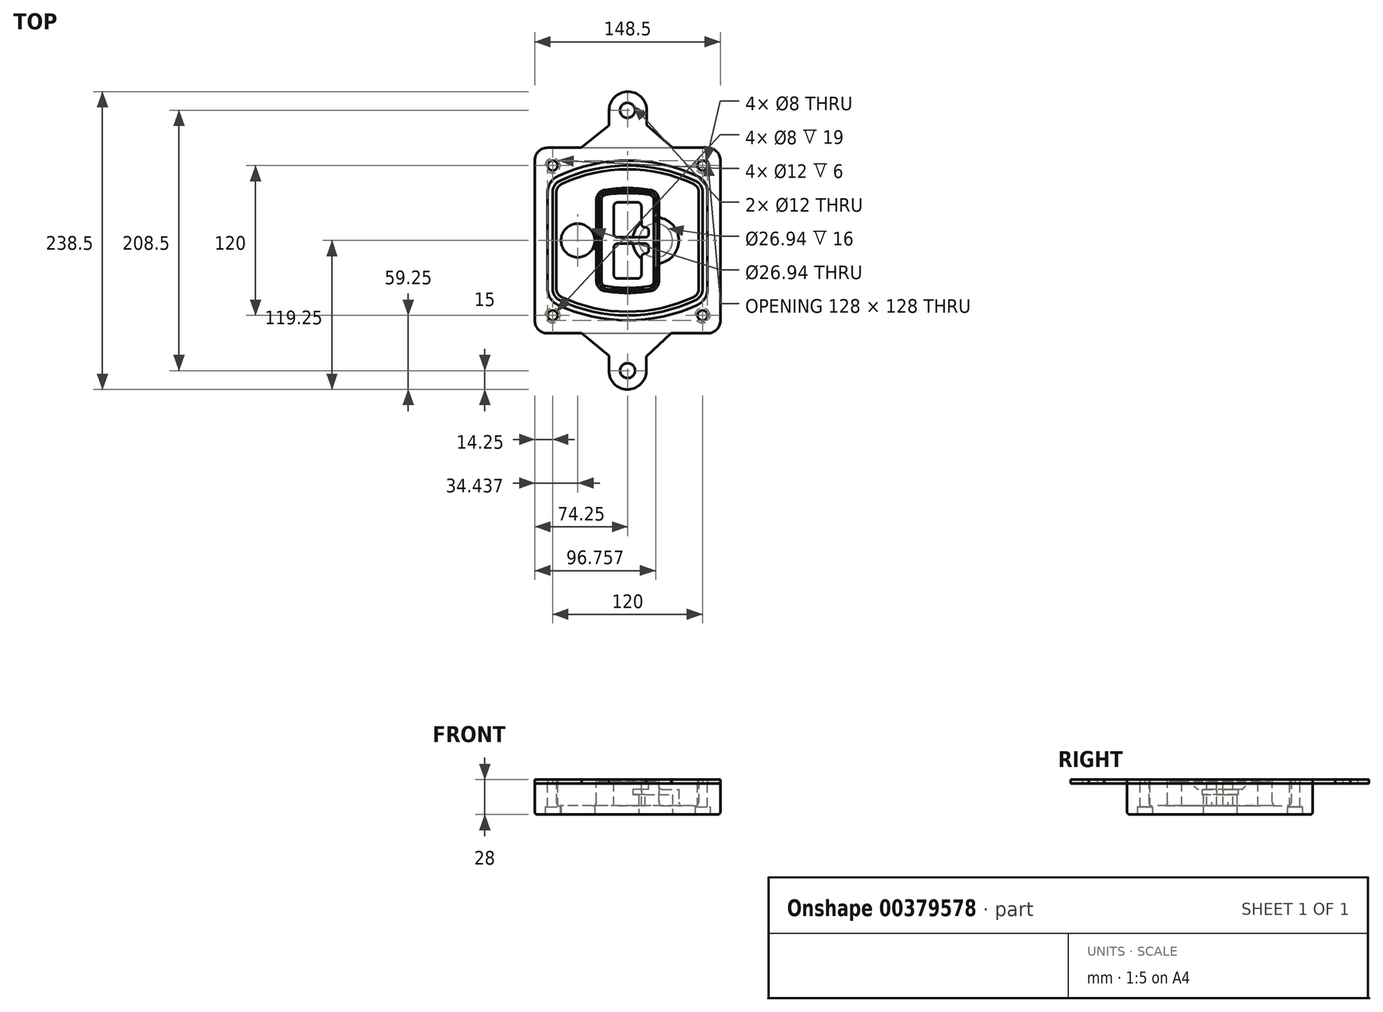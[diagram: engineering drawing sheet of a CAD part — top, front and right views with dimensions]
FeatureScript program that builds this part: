
annotation { "Feature Type Name" : "Feature", "Feature Type Description" : "" }
export const myFeature = defineFeature(function(context is Context, id is Id, definition is map)
    precondition{}
    {
        {
            var Q0;
            Q0=qCreatedBy(makeId("Top.planeOp"),FACE);
            var sketch = newSketch(context, id + "F0", { "sketchPlane" : qUnion([Q0])});
            skPoint(sketch, "E0.rect.middle", {"position": v(0, 0) * mm});
            skLineSegment(sketch, "E1.bottom", {"start": v(-64.25, -74.25) * mm, "end": v(64.25, -74.25) * mm});
            skLineSegment(sketch, "E1.top", {"start": v(-64.25, 74.25) * mm, "end": v(64.25, 74.25) * mm});
            skLineSegment(sketch, "E1.left", {"start": v(-74.25, -64.25) * mm, "end": v(-74.25, 64.25) * mm});
            skLineSegment(sketch, "E1.right", {"start": v(74.25, -64.25) * mm, "end": v(74.25, 64.25) * mm});
            skLineSegment(sketch, "E2", {"start": v(-74.25, 74.25) * mm, "end": v(74.25, -74.25) * mm, "construction": true});
            skLineSegment(sketch, "E3", {"start": v(74.25, 74.25) * mm, "end": v(-74.25, -74.25) * mm, "construction": true});
            skCircle(sketch, "E4", {"center": v(-60, 60) * mm, "radius": 4 * mm});
            skCircle(sketch, "E5", {"center": v(60, 60) * mm, "radius": 4 * mm});
            skCircle(sketch, "E6", {"center": v(60, -60) * mm, "radius": 4 * mm});
            skCircle(sketch, "E7", {"center": v(-60, -60) * mm, "radius": 4 * mm});
            skLineSegment(sketch, "E8", {"start": v(-60, 60) * mm, "end": v(60, 60) * mm, "construction": true});
            skLineSegment(sketch, "E9", {"start": v(60, 60) * mm, "end": v(60, -60) * mm, "construction": true});
            skLineSegment(sketch, "E10", {"start": v(60, -60) * mm, "end": v(-60, -60) * mm, "construction": true});
            skLineSegment(sketch, "E11", {"start": v(-60, -60) * mm, "end": v(-60, 60) * mm, "construction": true});
            skLineSegment(sketch, "E12", {"start": v(-60, 38.83) * mm, "end": v(-60, -38.83) * mm});
            skLineSegment(sketch, "E13", {"start": v(60, 38.83) * mm, "end": v(60, -38.83) * mm});
            skArc(sketch, "E14", {"start": v(54.26, 47.88) * mm, "mid": v(0, 60) * mm, "end": v(-54.26, 47.88) * mm});
            skArc(sketch, "E15", {"start": v(-54.26, -47.88) * mm, "mid": v(0, -60) * mm, "end": v(54.26, -47.88) * mm});
            skLineSegment(sketch, "E16", {"start": v(-60, 0) * mm, "end": v(60, 0) * mm, "construction": true});
            skPoint(sketch, "E17.visualSharp", {"position": v(-60, -45) * mm});
            skArc(sketch, "E17.filletArc", {"start": v(-60, -38.83) * mm, "mid": v(-58.44, -44.2) * mm, "end": v(-54.26, -47.88) * mm});
            skPoint(sketch, "E18.visualSharp", {"position": v(-60, 45) * mm});
            skArc(sketch, "E18.filletArc", {"start": v(-54.26, 47.88) * mm, "mid": v(-58.44, 44.2) * mm, "end": v(-60, 38.83) * mm});
            skPoint(sketch, "E19.visualSharp", {"position": v(60, 45) * mm});
            skArc(sketch, "E19.filletArc", {"start": v(60, 38.83) * mm, "mid": v(58.44, 44.2) * mm, "end": v(54.26, 47.88) * mm});
            skPoint(sketch, "E20.visualSharp", {"position": v(60, -45) * mm});
            skArc(sketch, "E20.filletArc", {"start": v(54.26, -47.88) * mm, "mid": v(58.44, -44.2) * mm, "end": v(60, -38.83) * mm});
            skPoint(sketch, "E21.visualSharp", {"position": v(-74.25, 74.25) * mm});
            skArc(sketch, "E21.filletArc", {"start": v(-64.25, 74.25) * mm, "mid": v(-71.32, 71.32) * mm, "end": v(-74.25, 64.25) * mm});
            skPoint(sketch, "E22.visualSharp", {"position": v(74.25, 74.25) * mm});
            skArc(sketch, "E22.filletArc", {"start": v(74.25, 64.25) * mm, "mid": v(71.32, 71.32) * mm, "end": v(64.25, 74.25) * mm});
            skPoint(sketch, "E23.visualSharp", {"position": v(74.25, -74.25) * mm});
            skArc(sketch, "E23.filletArc", {"start": v(64.25, -74.25) * mm, "mid": v(71.32, -71.32) * mm, "end": v(74.25, -64.25) * mm});
            skPoint(sketch, "E24.visualSharp", {"position": v(-74.25, -74.25) * mm});
            skArc(sketch, "E24.filletArc", {"start": v(-74.25, -64.25) * mm, "mid": v(-71.32, -71.32) * mm, "end": v(-64.25, -74.25) * mm});
            skArc(sketch, "E25.0", {"start": v(57, 38.83) * mm, "mid": v(55.9, 42.58) * mm, "end": v(52.98, 45.17) * mm});
            skLineSegment(sketch, "E25.1", {"start": v(57, 38.83) * mm, "end": v(57, -38.83) * mm});
            skArc(sketch, "E25.2", {"start": v(52.98, -45.17) * mm, "mid": v(55.9, -42.58) * mm, "end": v(57, -38.83) * mm});
            skArc(sketch, "E25.3", {"start": v(-52.98, -45.17) * mm, "mid": v(0, -57) * mm, "end": v(52.98, -45.17) * mm});
            skArc(sketch, "E25.4", {"start": v(-57, -38.83) * mm, "mid": v(-55.9, -42.58) * mm, "end": v(-52.98, -45.17) * mm});
            skArc(sketch, "E25.5", {"start": v(52.98, 45.17) * mm, "mid": v(0, 57) * mm, "end": v(-52.98, 45.17) * mm});
            skLineSegment(sketch, "E25.6", {"start": v(-57, 38.83) * mm, "end": v(-57, -38.83) * mm});
            skArc(sketch, "E25.7", {"start": v(-52.98, 45.17) * mm, "mid": v(-55.9, 42.58) * mm, "end": v(-57, 38.83) * mm});
            skArc(sketch, "E26.0", {"start": v(-55.96, 51.5) * mm, "mid": v(-61.82, 46.33) * mm, "end": v(-64, 38.83) * mm});
            skArc(sketch, "E26.1", {"start": v(55.96, 51.5) * mm, "mid": v(0, 64) * mm, "end": v(-55.96, 51.5) * mm});
            skArc(sketch, "E26.2", {"start": v(64, 38.83) * mm, "mid": v(61.82, 46.33) * mm, "end": v(55.96, 51.5) * mm});
            skLineSegment(sketch, "E26.3", {"start": v(64, 38.83) * mm, "end": v(64, -38.83) * mm});
            skArc(sketch, "E26.4", {"start": v(55.96, -51.5) * mm, "mid": v(61.82, -46.33) * mm, "end": v(64, -38.83) * mm});
            skLineSegment(sketch, "E26.5", {"start": v(-64, 38.83) * mm, "end": v(-64, -38.83) * mm});
            skArc(sketch, "E26.6", {"start": v(-55.96, -51.5) * mm, "mid": v(0, -64) * mm, "end": v(55.96, -51.5) * mm});
            skArc(sketch, "E26.7", {"start": v(-64, -38.83) * mm, "mid": v(-61.82, -46.33) * mm, "end": v(-55.96, -51.5) * mm});
            skPoint(sketch, "E27.endSnap0", {"position": v(0, 74.25) * mm});
            skLineSegment(sketch, "E28", {"start": v(0, 74.25) * mm, "end": v(0, 104.25) * mm});
            skCircle(sketch, "E29", {"center": v(0, 104.25) * mm, "radius": 6 * mm});
            skLineSegment(sketch, "E30", {"start": v(-37.03, 74.25) * mm, "end": v(-14.76, 92.25) * mm});
            skLineSegment(sketch, "E31", {"start": v(36.07, 74.25) * mm, "end": v(15.24, 92.42) * mm});
            skLineSegment(sketch, "E32", {"start": v(-14.76, 92.25) * mm, "end": v(-14.76, 104.25) * mm});
            skLineSegment(sketch, "E33", {"start": v(15.24, 92.42) * mm, "end": v(15.24, 104.42) * mm});
            skLineSegment(sketch, "E34", {"start": v(-60.73, 104.25) * mm, "end": v(-60.73, 74.25) * mm});
            skArc(sketch, "E35", {"start": v(-14.76, 104.25) * mm, "mid": v(0.16, 119.25) * mm, "end": v(15.24, 104.42) * mm});
            skLineSegment(sketch, "E36", {"start": v(0, -74.25) * mm, "end": v(0, -104.25) * mm});
            skCircle(sketch, "E37", {"center": v(0, -104.25) * mm, "radius": 6 * mm});
            skLineSegment(sketch, "E38", {"start": v(34.92, -74.25) * mm, "end": v(15, -92.78) * mm});
            skLineSegment(sketch, "E39", {"start": v(15, -92.78) * mm, "end": v(15, -104.78) * mm});
            skLineSegment(sketch, "E40", {"start": v(-36.77, -74.25) * mm, "end": v(-15, -92.25) * mm});
            skLineSegment(sketch, "E41", {"start": v(-15, -92.25) * mm, "end": v(-15, -104.25) * mm});
            skArc(sketch, "E42", {"start": v(-15, -104.25) * mm, "mid": v(-0.26, -119.25) * mm, "end": v(15, -104.78) * mm});
            skSolve(sketch);
        }
        {
            var Q0;
            Q0=makeQuery(id+"F0.imprint","IMPRINT",FACE,{"disambiguationData":[TD([[makeQuery(id+"F0.imprint","IMPRINT",EDGE,{"derivedFrom":sQuery(id+"F0.wireOp",EDGE,"E1.bottom")}),1.0]])]});
            var Q1;
            Q1=makeQuery(id+"F0.imprint","IMPRINT",FACE,{"disambiguationData":[TD([[makeQuery(id+"F0.imprint","IMPRINT",EDGE,{"derivedFrom":sQuery(id+"F0.wireOp",EDGE,"E12")}),1.0]])]});
            var Q2;
            Q2=makeQuery(id+"F0.imprint","IMPRINT",FACE,{"disambiguationData":[TD([[makeQuery(id+"F0.imprint","IMPRINT",EDGE,{"derivedFrom":sQuery(id+"F0.wireOp",EDGE,"E25.0")}),1.0]])]});
            var Q3;
            Q3=makeQuery(id+"F0.imprint","IMPRINT",FACE,{"disambiguationData":[TD([[makeQuery(id+"F0.imprint","IMPRINT",EDGE,{"derivedFrom":sQuery(id+"F0.wireOp",EDGE,"E12")}),-1.0]])]});
            extrude(context, id + "F1", {"entities" : qUnion([Q0, Q1, Q2, Q3]), "oppositeDirection" : true, "depth" : 25 * mm});
        }
        {
            var Q0;
            Q0=makeQuery(id+"F0.imprint","IMPRINT",FACE,{"disambiguationData":[TD([[makeQuery(id+"F0.imprint","IMPRINT",EDGE,{"derivedFrom":sQuery(id+"F0.wireOp",EDGE,"E12")}),1.0]])]});
            extrude(context, id + "F2", {"entities" : qUnion([Q0]), "operationType" : NewBodyOperationType.ADD, "depth" : 3 * mm});
        }
        {
            var Q0;
            Q0=makeQuery(id+"F0.imprint","IMPRINT",FACE,{"disambiguationData":[TD([[makeQuery(id+"F0.imprint","IMPRINT",EDGE,{"derivedFrom":sQuery(id+"F0.wireOp",EDGE,"E25.0")}),1.0]])]});
            extrude(context, id + "F3", {"entities" : qUnion([Q0]), "operationType" : NewBodyOperationType.REMOVE, "oppositeDirection" : true, "depth" : 18 * mm});
        }
        {
            var Q0;
            Q0=makeQuery(id+"F2.opExtrude","CAP_FACE",FACE,{"disambiguationData":[OSD([sQuery(id+"F0.wireOp",EDGE,"E12"),sQuery(id+"F0.wireOp",EDGE,"E13"),sQuery(id+"F0.wireOp",EDGE,"E14"),sQuery(id+"F0.wireOp",EDGE,"E15"),sQuery(id+"F0.wireOp",EDGE,"E17.filletArc"),sQuery(id+"F0.wireOp",EDGE,"E18.filletArc"),sQuery(id+"F0.wireOp",EDGE,"E19.filletArc"),sQuery(id+"F0.wireOp",EDGE,"E20.filletArc"),sQuery(id+"F0.wireOp",EDGE,"E25.0"),sQuery(id+"F0.wireOp",EDGE,"E25.1"),sQuery(id+"F0.wireOp",EDGE,"E25.2"),sQuery(id+"F0.wireOp",EDGE,"E25.3"),sQuery(id+"F0.wireOp",EDGE,"E25.4"),sQuery(id+"F0.wireOp",EDGE,"E25.5"),sQuery(id+"F0.wireOp",EDGE,"E25.6"),sQuery(id+"F0.wireOp",EDGE,"E25.7")])],"isStart":false});
            var sketch = newSketch(context, id + "F4", { "sketchPlane" : qUnion([Q0])});
            skArc(sketch, "E43.0", {"start": v(-18.34, -40.45) * mm, "mid": v(0, -42) * mm, "end": v(18.34, -40.45) * mm});
            skArc(sketch, "E44.0", {"start": v(18.34, 40.45) * mm, "mid": v(0, 42) * mm, "end": v(-18.34, 40.45) * mm});
            skLineSegment(sketch, "E45", {"start": v(-25, 32.57) * mm, "end": v(-25, -32.57) * mm});
            skLineSegment(sketch, "E46", {"start": v(25, 32.57) * mm, "end": v(25, -32.57) * mm});
            skLineSegment(sketch, "E47", {"start": v(-25, 39.1) * mm, "end": v(25, 39.1) * mm, "construction": true});
            skLineSegment(sketch, "E48", {"start": v(-25, -39.1) * mm, "end": v(25, -39.1) * mm, "construction": true});
            skPoint(sketch, "E49.visualSharp", {"position": v(-25, 39.1) * mm});
            skArc(sketch, "E49.filletArc", {"start": v(-18.34, 40.45) * mm, "mid": v(-23.11, 37.73) * mm, "end": v(-25, 32.57) * mm});
            skPoint(sketch, "E50.visualSharp", {"position": v(25, 39.1) * mm});
            skArc(sketch, "E50.filletArc", {"start": v(25, 32.57) * mm, "mid": v(23.11, 37.73) * mm, "end": v(18.34, 40.45) * mm});
            skPoint(sketch, "E51.visualSharp", {"position": v(25, -39.1) * mm});
            skArc(sketch, "E51.filletArc", {"start": v(18.34, -40.45) * mm, "mid": v(23.11, -37.73) * mm, "end": v(25, -32.57) * mm});
            skPoint(sketch, "E52.visualSharp", {"position": v(-25, -39.1) * mm});
            skArc(sketch, "E52.filletArc", {"start": v(-25, -32.57) * mm, "mid": v(-23.11, -37.73) * mm, "end": v(-18.34, -40.45) * mm});
            skArc(sketch, "E53.0", {"start": v(52.98, 45.17) * mm, "mid": v(0, 57) * mm, "end": v(-52.98, 45.17) * mm});
            skArc(sketch, "E53.1", {"start": v(-52.98, 45.17) * mm, "mid": v(-55.9, 42.58) * mm, "end": v(-57, 38.83) * mm});
            skLineSegment(sketch, "E53.2", {"start": v(-57, 38.83) * mm, "end": v(-57, -38.83) * mm});
            skArc(sketch, "E53.3", {"start": v(-57, -38.83) * mm, "mid": v(-55.9, -42.58) * mm, "end": v(-52.98, -45.17) * mm});
            skArc(sketch, "E53.4", {"start": v(-52.98, -45.17) * mm, "mid": v(0, -57) * mm, "end": v(52.98, -45.17) * mm});
            skArc(sketch, "E53.5", {"start": v(52.98, -45.17) * mm, "mid": v(55.9, -42.58) * mm, "end": v(57, -38.83) * mm});
            skLineSegment(sketch, "E53.6", {"start": v(57, 38.83) * mm, "end": v(57, -38.83) * mm});
            skArc(sketch, "E53.7", {"start": v(57, 38.83) * mm, "mid": v(55.9, 42.58) * mm, "end": v(52.98, 45.17) * mm});
            skLineSegment(sketch, "E54.0", {"start": v(23, 32.57) * mm, "end": v(23, -32.57) * mm});
            skArc(sketch, "E54.1", {"start": v(18, -38.48) * mm, "mid": v(21.58, -36.44) * mm, "end": v(23, -32.57) * mm});
            skArc(sketch, "E54.2", {"start": v(-18, -38.48) * mm, "mid": v(0, -40) * mm, "end": v(18, -38.48) * mm});
            skArc(sketch, "E54.3", {"start": v(-23, -32.57) * mm, "mid": v(-21.58, -36.44) * mm, "end": v(-18, -38.48) * mm});
            skLineSegment(sketch, "E54.4", {"start": v(-23, 32.57) * mm, "end": v(-23, -32.57) * mm});
            skArc(sketch, "E54.5", {"start": v(23, 32.57) * mm, "mid": v(21.58, 36.44) * mm, "end": v(18, 38.48) * mm});
            skArc(sketch, "E54.6", {"start": v(-18, 38.48) * mm, "mid": v(-21.58, 36.44) * mm, "end": v(-23, 32.57) * mm});
            skArc(sketch, "E54.7", {"start": v(18, 38.48) * mm, "mid": v(0, 40) * mm, "end": v(-18, 38.48) * mm});
            skArc(sketch, "E55.0", {"start": v(21, 32.57) * mm, "mid": v(20.06, 35.15) * mm, "end": v(17.67, 36.5) * mm});
            skLineSegment(sketch, "E55.1", {"start": v(21, 32.57) * mm, "end": v(21, -32.57) * mm});
            skArc(sketch, "E55.2", {"start": v(17.67, -36.5) * mm, "mid": v(20.06, -35.15) * mm, "end": v(21, -32.57) * mm});
            skArc(sketch, "E55.3", {"start": v(-17.67, -36.5) * mm, "mid": v(0, -38) * mm, "end": v(17.67, -36.5) * mm});
            skArc(sketch, "E55.4", {"start": v(-21, -32.57) * mm, "mid": v(-20.06, -35.15) * mm, "end": v(-17.67, -36.5) * mm});
            skArc(sketch, "E55.5", {"start": v(17.67, 36.5) * mm, "mid": v(0, 38) * mm, "end": v(-17.67, 36.5) * mm});
            skLineSegment(sketch, "E55.6", {"start": v(-21, 32.57) * mm, "end": v(-21, -32.57) * mm});
            skArc(sketch, "E55.7", {"start": v(-17.67, 36.5) * mm, "mid": v(-20.06, 35.15) * mm, "end": v(-21, 32.57) * mm});
            skLineSegment(sketch, "E56", {"start": v(-25, 0) * mm, "end": v(25, 0) * mm, "construction": true});
            skLineSegment(sketch, "E57", {"start": v(-11, 5.5) * mm, "end": v(-11, 27.5) * mm});
            skLineSegment(sketch, "E58", {"start": v(-8, 30.5) * mm, "end": v(8, 30.5) * mm});
            skLineSegment(sketch, "E59", {"start": v(11, 27.5) * mm, "end": v(11, 13.5) * mm});
            skLineSegment(sketch, "E60", {"start": v(14, 10.5) * mm, "end": v(14, 10.5) * mm});
            skLineSegment(sketch, "E61", {"start": v(17, 7.5) * mm, "end": v(17, 5.5) * mm});
            skLineSegment(sketch, "E62", {"start": v(14, 2.5) * mm, "end": v(-8, 2.5) * mm});
            skPoint(sketch, "E63.visualSharp", {"position": v(-11, 30.5) * mm});
            skArc(sketch, "E63.filletArc", {"start": v(-8, 30.5) * mm, "mid": v(-10.12, 29.62) * mm, "end": v(-11, 27.5) * mm});
            skPoint(sketch, "E64.visualSharp", {"position": v(11, 30.5) * mm});
            skArc(sketch, "E64.filletArc", {"start": v(11, 27.5) * mm, "mid": v(10.12, 29.62) * mm, "end": v(8, 30.5) * mm});
            skPoint(sketch, "E65.visualSharp", {"position": v(11, 10.5) * mm});
            skArc(sketch, "E65.filletArc", {"start": v(11, 13.5) * mm, "mid": v(11.88, 11.38) * mm, "end": v(14, 10.5) * mm});
            skPoint(sketch, "E66.visualSharp", {"position": v(17, 10.5) * mm});
            skArc(sketch, "E66.filletArc", {"start": v(17, 7.5) * mm, "mid": v(16.12, 9.62) * mm, "end": v(14, 10.5) * mm});
            skPoint(sketch, "E67.visualSharp", {"position": v(17, 2.5) * mm});
            skArc(sketch, "E67.filletArc", {"start": v(14, 2.5) * mm, "mid": v(16.12, 3.38) * mm, "end": v(17, 5.5) * mm});
            skPoint(sketch, "E68.visualSharp", {"position": v(-11, 2.5) * mm});
            skArc(sketch, "E68.filletArc", {"start": v(-11, 5.5) * mm, "mid": v(-10.12, 3.38) * mm, "end": v(-8, 2.5) * mm});
            skLineSegment(sketch, "E69.0.MirrorCS", {"start": v(14, -2.5) * mm, "end": v(-8, -2.5) * mm});
            skArc(sketch, "E70.0.MirrorCS", {"start": v(-11, -5.5) * mm, "mid": v(-10.12, -3.38) * mm, "end": v(-8, -2.5) * mm});
            skLineSegment(sketch, "E71.0.MirrorCS", {"start": v(-11, -5.5) * mm, "end": v(-11, -27.5) * mm});
            skArc(sketch, "E72.0.MirrorCS", {"start": v(-8, -30.5) * mm, "mid": v(-10.12, -29.62) * mm, "end": v(-11, -27.5) * mm});
            skLineSegment(sketch, "E73.0.MirrorCS", {"start": v(-8, -30.5) * mm, "end": v(8, -30.5) * mm});
            skArc(sketch, "E74.0.MirrorCS", {"start": v(11, -27.5) * mm, "mid": v(10.12, -29.62) * mm, "end": v(8, -30.5) * mm});
            skLineSegment(sketch, "E75.0.MirrorCS", {"start": v(11, -27.5) * mm, "end": v(11, -13.5) * mm});
            skArc(sketch, "E76.0.MirrorCS", {"start": v(11, -13.5) * mm, "mid": v(11.88, -11.38) * mm, "end": v(14, -10.5) * mm});
            skArc(sketch, "E77.0.MirrorCS", {"start": v(17, -7.5) * mm, "mid": v(16.12, -9.62) * mm, "end": v(14, -10.5) * mm});
            skLineSegment(sketch, "E78.0.MirrorCS", {"start": v(17, -7.5) * mm, "end": v(17, -5.5) * mm});
            skArc(sketch, "E79.0.MirrorCS", {"start": v(14, -2.5) * mm, "mid": v(16.12, -3.38) * mm, "end": v(17, -5.5) * mm});
            skSolve(sketch);
        }
        {
            var Q0;
            Q0=makeQuery(id+"F4.imprint","IMPRINT",FACE,{"disambiguationData":[TD([[makeQuery(id+"F4.imprint","IMPRINT",EDGE,{"derivedFrom":sQuery(id+"F4.wireOp",EDGE,"E43.0")}),1.0]])]});
            var Q1;
            Q1=makeQuery(id+"F4.imprint","IMPRINT",FACE,{"disambiguationData":[TD([[makeQuery(id+"F4.imprint","IMPRINT",EDGE,{"derivedFrom":sQuery(id+"F4.wireOp",EDGE,"E54.0")}),-1.0]])]});
            var Q2;
            Q2=makeQuery(id+"F4.imprint","IMPRINT",FACE,{"disambiguationData":[TD([[makeQuery(id+"F4.imprint","IMPRINT",EDGE,{"derivedFrom":sQuery(id+"F4.wireOp",EDGE,"E55.0")}),1.0]])]});
            extrude(context, id + "F5", {"entities" : qUnion([Q0, Q1, Q2]), "operationType" : NewBodyOperationType.ADD, "endBound" : BoundingType.UP_TO_NEXT, "oppositeDirection" : true, "depth" : 25 * mm});
        }
        {
            var Q0;
            Q0=makeQuery(id+"F4.imprint","IMPRINT",FACE,{"disambiguationData":[TD([[makeQuery(id+"F4.imprint","IMPRINT",EDGE,{"derivedFrom":sQuery(id+"F4.wireOp",EDGE,"E54.0")}),-1.0]])]});
            extrude(context, id + "F6", {"entities" : qUnion([Q0]), "operationType" : NewBodyOperationType.REMOVE, "oppositeDirection" : true, "depth" : 2 * mm});
        }
        {
            var Q0;
            Q0=makeQuery(id+"F1.opExtrude","CAP_FACE",FACE,{"disambiguationData":[OSD([sQuery(id+"F0.wireOp",EDGE,"E1.bottom"),sQuery(id+"F0.wireOp",EDGE,"E1.top"),sQuery(id+"F0.wireOp",EDGE,"E1.left"),sQuery(id+"F0.wireOp",EDGE,"E1.right"),sQuery(id+"F0.wireOp",EDGE,"E4"),sQuery(id+"F0.wireOp",EDGE,"E5"),sQuery(id+"F0.wireOp",EDGE,"E6"),sQuery(id+"F0.wireOp",EDGE,"E7"),sQuery(id+"F0.wireOp",EDGE,"E21.filletArc"),sQuery(id+"F0.wireOp",EDGE,"E22.filletArc"),sQuery(id+"F0.wireOp",EDGE,"E23.filletArc"),sQuery(id+"F0.wireOp",EDGE,"E24.filletArc")])],"isStart":false});
            var sketch = newSketch(context, id + "F7", { "sketchPlane" : qUnion([Q0])});
            skCircle(sketch, "E80", {"center": v(22.5, 0) * mm, "radius": 13.47 * mm});
            skCircle(sketch, "E81", {"center": v(-39.81, 0) * mm, "radius": 13.47 * mm});
            skLineSegment(sketch, "E82", {"start": v(74.25, 0) * mm, "end": v(-74.25, 0) * mm});
            skCircle(sketch, "E83", {"center": v(22.5, 0) * mm, "radius": 18.47 * mm});
            skCircle(sketch, "E84", {"center": v(60, -60) * mm, "radius": 6 * mm});
            skCircle(sketch, "E85", {"center": v(-60, -60) * mm, "radius": 6 * mm});
            skCircle(sketch, "E86", {"center": v(-60, 60) * mm, "radius": 6 * mm});
            skCircle(sketch, "E87", {"center": v(60, 60) * mm, "radius": 6 * mm});
            skSolve(sketch);
        }
        {
            var Q0;
            {var subQ1=sQuery(id+"F7.wireOp",EDGE,"E82");var subQ4=sQuery(id+"F7.wireOp",EDGE,"E80");var subQ6=makeQuery(id+"F7.imprint","INTERSECT",VERTEX,{"disambiguationData":[OD(0.0)],"derivedFrom":[subQ4,subQ1]});Q0=makeQuery(id+"F7.imprint","IMPRINT",FACE,{"disambiguationData":[TD([[makeQuery(id+"F7.imprint","IMPRINT",EDGE,{"disambiguationData":[TD([[subQ6,-1.0]])],"derivedFrom":subQ4}),-1.0]])]});}
            var Q1;
            {var subQ0=sQuery(id+"F7.wireOp",EDGE,"E82");var subQ1=sQuery(id+"F7.wireOp",EDGE,"E80");var subQ3=makeQuery(id+"F7.imprint","INTERSECT",VERTEX,{"disambiguationData":[OD(0.0)],"derivedFrom":[subQ1,subQ0]});Q1=makeQuery(id+"F7.imprint","IMPRINT",FACE,{"disambiguationData":[TD([[makeQuery(id+"F7.imprint","IMPRINT",EDGE,{"disambiguationData":[TD([[subQ3,-1.0]])],"derivedFrom":subQ1}),1.0]])]});}
            var Q2;
            {var subQ0=sQuery(id+"F7.wireOp",EDGE,"E82");var subQ1=sQuery(id+"F7.wireOp",EDGE,"E80");var subQ3=makeQuery(id+"F7.imprint","INTERSECT",VERTEX,{"disambiguationData":[OD(0.0)],"derivedFrom":[subQ1,subQ0]});Q2=makeQuery(id+"F7.imprint","IMPRINT",FACE,{"disambiguationData":[TD([[makeQuery(id+"F7.imprint","IMPRINT",EDGE,{"disambiguationData":[TD([[subQ3,1.0]])],"derivedFrom":subQ1}),1.0]])]});}
            var Q3;
            {var subQ1=sQuery(id+"F7.wireOp",EDGE,"E82");var subQ4=sQuery(id+"F7.wireOp",EDGE,"E80");var subQ6=makeQuery(id+"F7.imprint","INTERSECT",VERTEX,{"disambiguationData":[OD(0.0)],"derivedFrom":[subQ4,subQ1]});Q3=makeQuery(id+"F7.imprint","IMPRINT",FACE,{"disambiguationData":[TD([[makeQuery(id+"F7.imprint","IMPRINT",EDGE,{"disambiguationData":[TD([[subQ6,1.0]])],"derivedFrom":subQ4}),-1.0]])]});}
            extrude(context, id + "F8", {"entities" : qUnion([Q0, Q1, Q2, Q3]), "operationType" : NewBodyOperationType.ADD, "oppositeDirection" : true, "depth" : 20 * mm});
        }
        {
            var Q0;
            {var subQ0=sQuery(id+"F7.wireOp",EDGE,"E82");var subQ1=sQuery(id+"F7.wireOp",EDGE,"E80");var subQ3=makeQuery(id+"F7.imprint","INTERSECT",VERTEX,{"disambiguationData":[OD(0.0)],"derivedFrom":[subQ1,subQ0]});Q0=makeQuery(id+"F7.imprint","IMPRINT",FACE,{"disambiguationData":[TD([[makeQuery(id+"F7.imprint","IMPRINT",EDGE,{"disambiguationData":[TD([[subQ3,-1.0]])],"derivedFrom":subQ1}),1.0]])]});}
            var Q1;
            {var subQ0=sQuery(id+"F7.wireOp",EDGE,"E82");var subQ1=sQuery(id+"F7.wireOp",EDGE,"E80");var subQ3=makeQuery(id+"F7.imprint","INTERSECT",VERTEX,{"disambiguationData":[OD(0.0)],"derivedFrom":[subQ1,subQ0]});Q1=makeQuery(id+"F7.imprint","IMPRINT",FACE,{"disambiguationData":[TD([[makeQuery(id+"F7.imprint","IMPRINT",EDGE,{"disambiguationData":[TD([[subQ3,1.0]])],"derivedFrom":subQ1}),1.0]])]});}
            extrude(context, id + "F9", {"entities" : qUnion([Q0, Q1]), "operationType" : NewBodyOperationType.REMOVE, "oppositeDirection" : true, "depth" : 16 * mm});
        }
        {
            var Q0;
            {var subQ0=sQuery(id+"F7.wireOp",EDGE,"E82");var subQ1=sQuery(id+"F7.wireOp",EDGE,"E81");var subQ3=makeQuery(id+"F7.imprint","INTERSECT",VERTEX,{"disambiguationData":[OD(0.0)],"derivedFrom":[subQ1,subQ0]});Q0=makeQuery(id+"F7.imprint","IMPRINT",FACE,{"disambiguationData":[TD([[makeQuery(id+"F7.imprint","IMPRINT",EDGE,{"disambiguationData":[TD([[subQ3,-1.0]])],"derivedFrom":subQ1}),1.0]])]});}
            var Q1;
            {var subQ0=sQuery(id+"F7.wireOp",EDGE,"E82");var subQ1=sQuery(id+"F7.wireOp",EDGE,"E81");var subQ3=makeQuery(id+"F7.imprint","INTERSECT",VERTEX,{"disambiguationData":[OD(0.0)],"derivedFrom":[subQ1,subQ0]});Q1=makeQuery(id+"F7.imprint","IMPRINT",FACE,{"disambiguationData":[TD([[makeQuery(id+"F7.imprint","IMPRINT",EDGE,{"disambiguationData":[TD([[subQ3,1.0]])],"derivedFrom":subQ1}),1.0]])]});}
            extrude(context, id + "F10", {"entities" : qUnion([Q0, Q1]), "operationType" : NewBodyOperationType.REMOVE, "oppositeDirection" : true, "depth" : 25 * mm});
        }
        {
            var Q0;
            Q0=makeQuery(id+"F7.imprint","IMPRINT",FACE,{"disambiguationData":[TD([[makeQuery(id+"F7.imprint","IMPRINT",EDGE,{"derivedFrom":sQuery(id+"F7.wireOp",EDGE,"E84")}),1.0]])]});
            var Q1;
            Q1=makeQuery(id+"F7.imprint","IMPRINT",FACE,{"disambiguationData":[TD([[makeQuery(id+"F7.imprint","IMPRINT",EDGE,{"derivedFrom":makeQuery(id+"F1.opExtrude","CAP_EDGE",EDGE,{"disambiguationData":[OSD([sQuery(id+"F0.wireOp",EDGE,"E5")])],"isStart":false})}),-1.0]])]});
            var Q2;
            Q2=makeQuery(id+"F7.imprint","IMPRINT",FACE,{"disambiguationData":[TD([[makeQuery(id+"F7.imprint","IMPRINT",EDGE,{"derivedFrom":sQuery(id+"F7.wireOp",EDGE,"E85")}),1.0]])]});
            var Q3;
            Q3=makeQuery(id+"F7.imprint","IMPRINT",FACE,{"disambiguationData":[TD([[makeQuery(id+"F7.imprint","IMPRINT",EDGE,{"derivedFrom":makeQuery(id+"F1.opExtrude","CAP_EDGE",EDGE,{"disambiguationData":[OSD([sQuery(id+"F0.wireOp",EDGE,"E4")])],"isStart":false})}),-1.0]])]});
            var Q4;
            Q4=makeQuery(id+"F7.imprint","IMPRINT",FACE,{"disambiguationData":[TD([[makeQuery(id+"F7.imprint","IMPRINT",EDGE,{"derivedFrom":sQuery(id+"F7.wireOp",EDGE,"E86")}),1.0]])]});
            var Q5;
            Q5=makeQuery(id+"F7.imprint","IMPRINT",FACE,{"disambiguationData":[TD([[makeQuery(id+"F7.imprint","IMPRINT",EDGE,{"derivedFrom":makeQuery(id+"F1.opExtrude","CAP_EDGE",EDGE,{"disambiguationData":[OSD([sQuery(id+"F0.wireOp",EDGE,"E7")])],"isStart":false})}),-1.0]])]});
            var Q6;
            Q6=makeQuery(id+"F7.imprint","IMPRINT",FACE,{"disambiguationData":[TD([[makeQuery(id+"F7.imprint","IMPRINT",EDGE,{"derivedFrom":sQuery(id+"F7.wireOp",EDGE,"E87")}),1.0]])]});
            var Q7;
            Q7=makeQuery(id+"F7.imprint","IMPRINT",FACE,{"disambiguationData":[TD([[makeQuery(id+"F7.imprint","IMPRINT",EDGE,{"derivedFrom":makeQuery(id+"F1.opExtrude","CAP_EDGE",EDGE,{"disambiguationData":[OSD([sQuery(id+"F0.wireOp",EDGE,"E6")])],"isStart":false})}),-1.0]])]});
            extrude(context, id + "F11", {"entities" : qUnion([Q0, Q1, Q2, Q3, Q4, Q5, Q6, Q7]), "operationType" : NewBodyOperationType.REMOVE, "oppositeDirection" : true, "depth" : 6 * mm});
        }
        {
            var Q0;
            Q0=makeQuery(id+"F9.boolean.opBoolean","COPY",FACE,{"derivedFrom":makeQuery(id+"F9.opExtrude","CAP_FACE",FACE,{"disambiguationData":[OSD([sQuery(id+"F7.wireOp",EDGE,"E80")])],"isStart":false})});
            var sketch = newSketch(context, id + "F12", { "sketchPlane" : qUnion([Q0])});
            skArc(sketch, "E88.0", {"start": v(11, 14.45) * mm, "mid": v(6.45, 9.13) * mm, "end": v(4.2, 2.5) * mm});
            skArc(sketch, "E88.1", {"start": v(4.2, -2.5) * mm, "mid": v(6.45, -9.13) * mm, "end": v(11, -14.45) * mm});
            skLineSegment(sketch, "E89", {"start": v(4.2, -2.5) * mm, "end": v(14, -2.5) * mm});
            skLineSegment(sketch, "E90.0", {"start": v(14, 2.5) * mm, "end": v(4.2, 2.5) * mm});
            skArc(sketch, "E90.1", {"start": v(14, 2.5) * mm, "mid": v(16.12, 3.38) * mm, "end": v(17, 5.5) * mm});
            skLineSegment(sketch, "E90.2", {"start": v(17, 7.5) * mm, "end": v(17, 5.5) * mm});
            skArc(sketch, "E90.3", {"start": v(17, 7.5) * mm, "mid": v(16.12, 9.62) * mm, "end": v(14, 10.5) * mm});
            skArc(sketch, "E90.4", {"start": v(11, 13.5) * mm, "mid": v(11.88, 11.38) * mm, "end": v(14, 10.5) * mm});
            skLineSegment(sketch, "E90.5", {"start": v(11, 14.45) * mm, "end": v(11, 13.5) * mm});
            skLineSegment(sketch, "E90.7", {"start": v(14, -2.5) * mm, "end": v(4.2, -2.5) * mm});
            skArc(sketch, "E90.8", {"start": v(14, -2.5) * mm, "mid": v(16.12, -3.38) * mm, "end": v(17, -5.5) * mm});
            skLineSegment(sketch, "E90.9", {"start": v(17, -7.5) * mm, "end": v(17, -5.5) * mm});
            skArc(sketch, "E90.10", {"start": v(17, -7.5) * mm, "mid": v(16.12, -9.62) * mm, "end": v(14, -10.5) * mm});
            skArc(sketch, "E90.11", {"start": v(11, -13.5) * mm, "mid": v(11.88, -11.38) * mm, "end": v(14, -10.5) * mm});
            skLineSegment(sketch, "E90.12", {"start": v(11, -14.45) * mm, "end": v(11, -13.5) * mm});
            skPoint(sketch, "E91.orphan", {"position": v(11, -27.5) * mm});
            skPoint(sketch, "E92.orphan", {"position": v(-8, -2.5) * mm});
            skPoint(sketch, "E93.orphan", {"position": v(-8, 2.5) * mm});
            skPoint(sketch, "E94.orphan", {"position": v(11, 27.5) * mm});
            skSolve(sketch);
        }
        {
            var Q0;
            {var subQ7=sQuery(id+"F12.wireOp",EDGE,"E88.0");var subQ14=sQuery(id+"F12.wireOp",EDGE,"E88.1");var subQ16=sQuery(id+"F12.wireOp",EDGE,"E90.1");var subQ18=sQuery(id+"F12.wireOp",EDGE,"E90.8");Q0=qUnion([makeQuery(id+"F12.imprint","IMPRINT",FACE,{"disambiguationData":[TD([[makeQuery(id+"F12.imprint","IMPRINT",EDGE,{"derivedFrom":subQ7}),1.0]])]}),makeQuery(id+"F12.imprint","IMPRINT",FACE,{"disambiguationData":[TD([[makeQuery(id+"F12.imprint","IMPRINT",EDGE,{"derivedFrom":subQ14}),1.0]])]}),makeQuery(id+"F12.imprint","IMPRINT",FACE,{"disambiguationData":[TD([[makeQuery(id+"F12.imprint","IMPRINT",EDGE,{"derivedFrom":subQ16}),1.0]])]}),makeQuery(id+"F12.imprint","IMPRINT",FACE,{"disambiguationData":[TD([[makeQuery(id+"F12.imprint","IMPRINT",EDGE,{"derivedFrom":subQ18}),-1.0]])]})]);}
            var Q1;
            Q1=makeQuery(id+"F5.boolean.opBoolean","SPLIT",FACE,{"disambiguationData":[TD([makeQuery(id+"F5.opExtrude","SWEPT_FACE",FACE,{"disambiguationData":[OSD([sQuery(id+"F4.wireOp",EDGE,"E57")])]})])],"derivedFrom":makeQuery(id+"F3.boolean.opBoolean","COPY",FACE,{"derivedFrom":makeQuery(id+"F3.opExtrude","CAP_FACE",FACE,{"disambiguationData":[OSD([sQuery(id+"F0.wireOp",EDGE,"E25.0"),sQuery(id+"F0.wireOp",EDGE,"E25.1"),sQuery(id+"F0.wireOp",EDGE,"E25.2"),sQuery(id+"F0.wireOp",EDGE,"E25.3"),sQuery(id+"F0.wireOp",EDGE,"E25.4"),sQuery(id+"F0.wireOp",EDGE,"E25.5"),sQuery(id+"F0.wireOp",EDGE,"E25.6"),sQuery(id+"F0.wireOp",EDGE,"E25.7")])],"isStart":false})})});
            extrude(context, id + "F13", {"entities" : qUnion([Q0]), "operationType" : NewBodyOperationType.REMOVE, "endBound" : BoundingType.UP_TO_SURFACE, "endBoundEntityFace" : qUnion([Q1]), "depth" : 25 * mm});
        }
        {
            var Q0;
            Q0=makeQuery(id+"F3.boolean.opBoolean","COPY",EDGE,{"derivedFrom":makeQuery(id+"F3.opExtrude","CAP_EDGE",EDGE,{"disambiguationData":[OSD([sQuery(id+"F0.wireOp",EDGE,"E25.6")])],"isStart":false})});
            var Q1;
            Q1=makeQuery(id+"F8.boolean.opBoolean","INTERSECT",EDGE,{"derivedFrom":[makeQuery(id+"F5.opExtrude","SWEPT_FACE",FACE,{"disambiguationData":[OSD([sQuery(id+"F4.wireOp",EDGE,"E46")])]}),makeQuery(id+"F8.opExtrude","CAP_FACE",FACE,{"disambiguationData":[OSD([sQuery(id+"F7.wireOp",EDGE,"E83")])],"isStart":false})]});
            var Q2;
            Q2=makeQuery(id+"F8.boolean.opBoolean","INTERSECT",EDGE,{"disambiguationData":[OD(1.0)],"derivedFrom":[makeQuery(id+"F5.opExtrude","SWEPT_FACE",FACE,{"disambiguationData":[OSD([sQuery(id+"F4.wireOp",EDGE,"E46")])]}),makeQuery(id+"F8.opExtrude","SWEPT_FACE",FACE,{"disambiguationData":[OSD([sQuery(id+"F7.wireOp",EDGE,"E83")])]})]});
            var Q3;
            {var subQ0=sQuery(id+"F4.wireOp",EDGE,"E46");Q3=makeQuery(id+"F8.boolean.opBoolean","SPLIT",EDGE,{"disambiguationData":[TD([makeQuery(id+"F5.opExtrude","SWEPT_FACE",FACE,{"disambiguationData":[OSD([sQuery(id+"F4.wireOp",EDGE,"E51.filletArc")])]})])],"derivedFrom":makeQuery(id+"F5.opExtrude","CAP_EDGE",EDGE,{"disambiguationData":[OSD([subQ0])],"isStart":false})});}
            var Q4;
            {var subQ0=sQuery(id+"F0.wireOp",EDGE,"E25.7");var subQ1=sQuery(id+"F0.wireOp",EDGE,"E25.1");var subQ2=sQuery(id+"F0.wireOp",EDGE,"E25.6");var subQ3=sQuery(id+"F0.wireOp",EDGE,"E25.5");var subQ4=sQuery(id+"F0.wireOp",EDGE,"E25.4");var subQ5=sQuery(id+"F0.wireOp",EDGE,"E25.0");var subQ6=sQuery(id+"F0.wireOp",EDGE,"E25.2");var subQ7=sQuery(id+"F0.wireOp",EDGE,"E25.3");Q4=makeQuery(id+"F8.boolean.opBoolean","INTERSECT",EDGE,{"derivedFrom":[makeQuery(id+"F5.boolean.opBoolean","SPLIT",FACE,{"disambiguationData":[TD([makeQuery(id+"F2.opExtrude","SWEPT_FACE",FACE,{"disambiguationData":[OSD([subQ5])]})])],"derivedFrom":makeQuery(id+"F3.boolean.opBoolean","COPY",FACE,{"derivedFrom":makeQuery(id+"F3.opExtrude","CAP_FACE",FACE,{"disambiguationData":[OSD([subQ5,subQ1,subQ6,subQ7,subQ4,subQ3,subQ2,subQ0])],"isStart":false})})}),makeQuery(id+"F8.opExtrude","SWEPT_FACE",FACE,{"disambiguationData":[OSD([sQuery(id+"F7.wireOp",EDGE,"E83")])]})]});}
            var Q5;
            Q5=makeQuery(id+"F8.boolean.opBoolean","INTERSECT",EDGE,{"disambiguationData":[OD(0.0)],"derivedFrom":[makeQuery(id+"F5.opExtrude","SWEPT_FACE",FACE,{"disambiguationData":[OSD([sQuery(id+"F4.wireOp",EDGE,"E46")])]}),makeQuery(id+"F8.opExtrude","SWEPT_FACE",FACE,{"disambiguationData":[OSD([sQuery(id+"F7.wireOp",EDGE,"E83")])]})]});
            fillet(context, id + "F14", {"entities" : qUnion([Q0, Q1, Q2, Q3, Q4, Q5]), "radius" : 3 * mm, "tangentPropagation" : true, "allowEdgeOverflow" : false});
        }
        {
            var Q0;
            Q0=makeQuery(id+"F1.opExtrude","CAP_EDGE",EDGE,{"disambiguationData":[OSD([sQuery(id+"F0.wireOp",EDGE,"E1.bottom")])],"isStart":false});
            fillet(context, id + "F15", {"entities" : qUnion([Q0]), "radius" : 2 * mm, "tangentPropagation" : true, "allowEdgeOverflow" : false});
        }
        {
            var Q0;
            Q0 = qSketchRegion(id + "F0", true);
            extrude(context, id + "F16", {"entities" : qUnion([Q0]), "depth" : 3 * mm});
        }
    });
